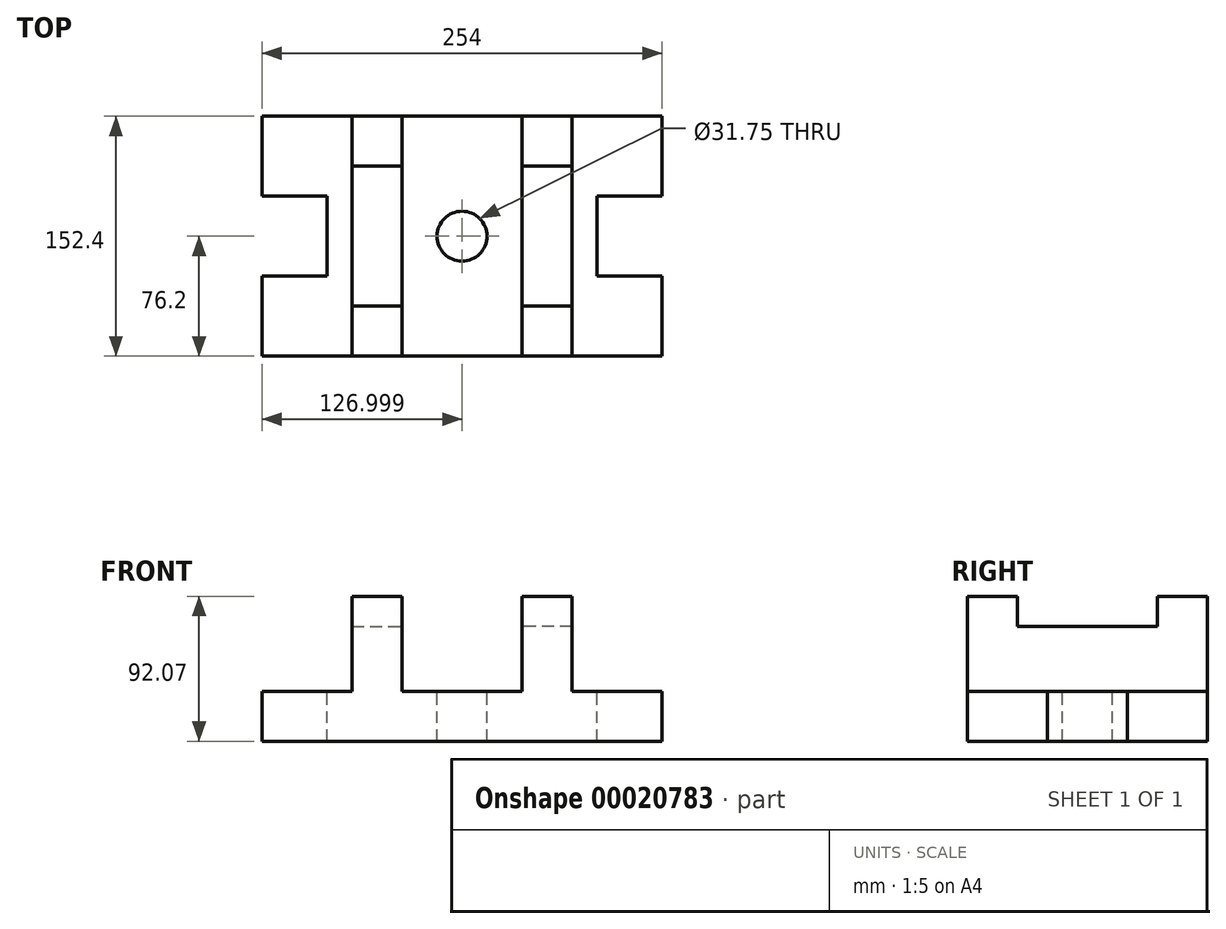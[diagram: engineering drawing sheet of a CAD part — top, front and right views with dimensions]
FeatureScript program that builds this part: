
annotation { "Feature Type Name" : "Feature", "Feature Type Description" : "" }
export const myFeature = defineFeature(function(context is Context, id is Id, definition is map)
    precondition{}
    {
        {
            var Q0;
            Q0=qCreatedBy(makeId("Front.planeOp"),FACE);
            var sketch = newSketch(context, id + "F0", { "sketchPlane" : qUnion([Q0])});
            skLineSegment(sketch, "E0.bottom", {"start": v(-66.2, -0.6) * mm, "end": v(60.8, -0.6) * mm});
            skLineSegment(sketch, "E0.top", {"start": v(-66.2, -32.34) * mm, "end": v(60.8, -32.34) * mm});
            skLineSegment(sketch, "E0.left", {"start": v(-66.2, -0.6) * mm, "end": v(-66.2, -32.34) * mm});
            skLineSegment(sketch, "E0.right", {"start": v(60.8, -0.6) * mm, "end": v(60.8, -32.34) * mm});
            skLineSegment(sketch, "E1.bottom", {"start": v(60.8, -32.34) * mm, "end": v(22.7, -32.34) * mm});
            skLineSegment(sketch, "E2", {"start": v(-66.2, -32.34) * mm, "end": v(-9.05, -32.34) * mm});
            skLineSegment(sketch, "E3", {"start": v(22.7, -32.34) * mm, "end": v(60.8, -32.34) * mm});
            skLineSegment(sketch, "E4.bottom", {"start": v(22.7, -32.34) * mm, "end": v(-9.05, -32.34) * mm});
            skLineSegment(sketch, "E4.top", {"start": v(22.7, 59.73) * mm, "end": v(-9.05, 59.73) * mm});
            skLineSegment(sketch, "E4.left", {"start": v(22.7, -32.34) * mm, "end": v(22.7, 59.73) * mm});
            skLineSegment(sketch, "E4.right", {"start": v(-9.05, -32.34) * mm, "end": v(-9.05, 59.73) * mm});
            skSolve(sketch);
        }
        {
            var Q0;
            Q0 = qSketchRegion(id + "F0", true);
            extrude(context, id + "F1", {"entities" : qUnion([Q0]), "depth" : 76.2 * mm});
        }
        {
            var Q0;
            {var subQ0=sQuery(id+"F0.wireOp",EDGE,"E0.bottom");Q0=makeQuery(id+"F1.opExtrude","SWEPT_FACE",FACE,{"disambiguationData":[OSD([subQ0]),TDD([makeQuery(id+"F0.imprint","IMPRINT",EDGE,{"disambiguationData":[TD([[makeQuery(id+"F0.imprint","INTERSECT",VERTEX,{"derivedFrom":[subQ0,sQuery(id+"F0.wireOp",EDGE,"E0.left")]}),-1.0]])],"derivedFrom":subQ0})])]});}
            var sketch = newSketch(context, id + "F2", { "sketchPlane" : qUnion([Q0])});
            skLineSegment(sketch, "E5.bottom", {"start": v(-66.2, 0) * mm, "end": v(-24.93, 0) * mm});
            skLineSegment(sketch, "E5.top", {"start": v(-66.2, -25.4) * mm, "end": v(-24.93, -25.4) * mm});
            skLineSegment(sketch, "E5.left", {"start": v(-66.2, 0) * mm, "end": v(-66.2, -25.4) * mm});
            skLineSegment(sketch, "E5.right", {"start": v(-24.93, 0) * mm, "end": v(-24.93, -25.4) * mm});
            skSolve(sketch);
        }
        {
            var Q0;
            Q0 = qSketchRegion(id + "F2", true);
            extrude(context, id + "F3", {"entities" : qUnion([Q0]), "operationType" : NewBodyOperationType.REMOVE, "oppositeDirection" : true, "depth" : 31.75 * mm});
        }
        {
            var Q0;
            Q0=makeQuery(id+"F1.opExtrude","SWEPT_FACE",FACE,{"disambiguationData":[OSD([sQuery(id+"F0.wireOp",EDGE,"E4.top")])]});
            var sketch = newSketch(context, id + "F4", { "sketchPlane" : qUnion([Q0])});
            skLineSegment(sketch, "E6.bottom", {"start": v(-9.05, 0) * mm, "end": v(22.7, 0) * mm});
            skLineSegment(sketch, "E6.top", {"start": v(-9.05, -44.45) * mm, "end": v(22.7, -44.45) * mm});
            skLineSegment(sketch, "E6.left", {"start": v(-9.05, 0) * mm, "end": v(-9.05, -44.45) * mm});
            skLineSegment(sketch, "E6.right", {"start": v(22.7, 0) * mm, "end": v(22.7, -44.45) * mm});
            skSolve(sketch);
        }
        {
            var Q0;
            Q0 = qSketchRegion(id + "F4", true);
            extrude(context, id + "F5", {"entities" : qUnion([Q0]), "operationType" : NewBodyOperationType.REMOVE, "oppositeDirection" : true, "depth" : 19.05 * mm});
        }
        {
            var Q0;
            Q0=makeQuery(id+"F1.opExtrude","SWEPT_BODY",BODY,{"disambiguationData":[OSD([sQuery(id+"F0.wireOp",EDGE,"E0.bottom"),sQuery(id+"F0.wireOp",EDGE,"E0.left"),sQuery(id+"F0.wireOp",EDGE,"E0.right"),sQuery(id+"F0.wireOp",EDGE,"E2"),sQuery(id+"F0.wireOp",EDGE,"E3"),sQuery(id+"F0.wireOp",EDGE,"E4.bottom"),sQuery(id+"F0.wireOp",EDGE,"E4.top"),sQuery(id+"F0.wireOp",EDGE,"E4.left"),sQuery(id+"F0.wireOp",EDGE,"E4.right")])]});
            var Q1;
            Q1=makeQuery(id+"F1.opExtrude","CAP_FACE",FACE,{"disambiguationData":[OSD([sQuery(id+"F0.wireOp",EDGE,"E0.bottom"),sQuery(id+"F0.wireOp",EDGE,"E0.left"),sQuery(id+"F0.wireOp",EDGE,"E0.right"),sQuery(id+"F0.wireOp",EDGE,"E2"),sQuery(id+"F0.wireOp",EDGE,"E3"),sQuery(id+"F0.wireOp",EDGE,"E4.bottom"),sQuery(id+"F0.wireOp",EDGE,"E4.top"),sQuery(id+"F0.wireOp",EDGE,"E4.left"),sQuery(id+"F0.wireOp",EDGE,"E4.right")])],"isStart":true});
            mirror(context, id + "F6", {"operationType" : NewBodyOperationType.ADD, "entities" : qUnion([Q0]), "mirrorPlane" : qUnion([Q1])});
        }
        {
            var Q0;
            Q0=makeQuery(id+"F1.opExtrude","SWEPT_BODY",BODY,{"disambiguationData":[OSD([sQuery(id+"F0.wireOp",EDGE,"E0.bottom"),sQuery(id+"F0.wireOp",EDGE,"E0.left"),sQuery(id+"F0.wireOp",EDGE,"E0.right"),sQuery(id+"F0.wireOp",EDGE,"E2"),sQuery(id+"F0.wireOp",EDGE,"E3"),sQuery(id+"F0.wireOp",EDGE,"E4.bottom"),sQuery(id+"F0.wireOp",EDGE,"E4.top"),sQuery(id+"F0.wireOp",EDGE,"E4.left"),sQuery(id+"F0.wireOp",EDGE,"E4.right")])]});
            var Q1;
            {var subQ0=makeQuery(id+"F1.opExtrude","SWEPT_FACE",FACE,{"disambiguationData":[OSD([sQuery(id+"F0.wireOp",EDGE,"E0.right")])]});Q1=makeQuery(id+"F6.boolean.opBoolean","MERGE",FACE,{"derivedFrom":[subQ0,makeQuery(id+"F6.opPattern","COPY",FACE,{"derivedFrom":subQ0,"instanceName":"1"})]});}
            mirror(context, id + "F7", {"operationType" : NewBodyOperationType.ADD, "entities" : qUnion([Q0]), "mirrorPlane" : qUnion([Q1])});
        }
        {
            var Q0;
            {var subQ0=sQuery(id+"F0.wireOp",EDGE,"E0.bottom");var subQ1=makeQuery(id+"F1.opExtrude","SWEPT_FACE",FACE,{"disambiguationData":[OSD([subQ0]),TDD([makeQuery(id+"F0.imprint","IMPRINT",EDGE,{"disambiguationData":[TD([[makeQuery(id+"F0.imprint","INTERSECT",VERTEX,{"derivedFrom":[subQ0,sQuery(id+"F0.wireOp",EDGE,"E0.right")]}),1.0]])],"derivedFrom":subQ0})])]});var subQ2=makeQuery(id+"F6.boolean.opBoolean","MERGE",FACE,{"derivedFrom":[subQ1,makeQuery(id+"F6.opPattern","COPY",FACE,{"derivedFrom":subQ1,"instanceName":"1"})]});Q0=makeQuery(id+"F7.boolean.opBoolean","MERGE",FACE,{"derivedFrom":[subQ2,makeQuery(id+"F7.opPattern","COPY",FACE,{"derivedFrom":subQ2,"instanceName":"1"})]});}
            var sketch = newSketch(context, id + "F8", { "sketchPlane" : qUnion([Q0])});
            skPoint(sketch, "E7", {"position": v(60.8, 0) * mm});
            skPoint(sketch, "E8.start.orphan", {"position": v(98.9, 76.2) * mm});
            skPoint(sketch, "E9.start.orphan", {"position": v(22.7, -76.2) * mm});
            skSolve(sketch);
        }
        {
            var Q0;
            Q0=sQuery(id+"F8.wireOp",VERTEX,"E7");
            var Q1;
            Q1=makeQuery(id+"F1.opExtrude","SWEPT_BODY",BODY,{"disambiguationData":[OSD([sQuery(id+"F0.wireOp",EDGE,"E0.bottom"),sQuery(id+"F0.wireOp",EDGE,"E0.left"),sQuery(id+"F0.wireOp",EDGE,"E0.right"),sQuery(id+"F0.wireOp",EDGE,"E2"),sQuery(id+"F0.wireOp",EDGE,"E3"),sQuery(id+"F0.wireOp",EDGE,"E4.bottom"),sQuery(id+"F0.wireOp",EDGE,"E4.top"),sQuery(id+"F0.wireOp",EDGE,"E4.left"),sQuery(id+"F0.wireOp",EDGE,"E4.right")])]});
            hole(context, id + "F9", {"style" : HoleStyle.SIMPLE, "holeDiameter" : 31.75 * mm, "endStyle" : HoleEndStyle.THROUGH, "locations" : qUnion([Q0]), "scope" : qUnion([Q1])});
        }
    });
